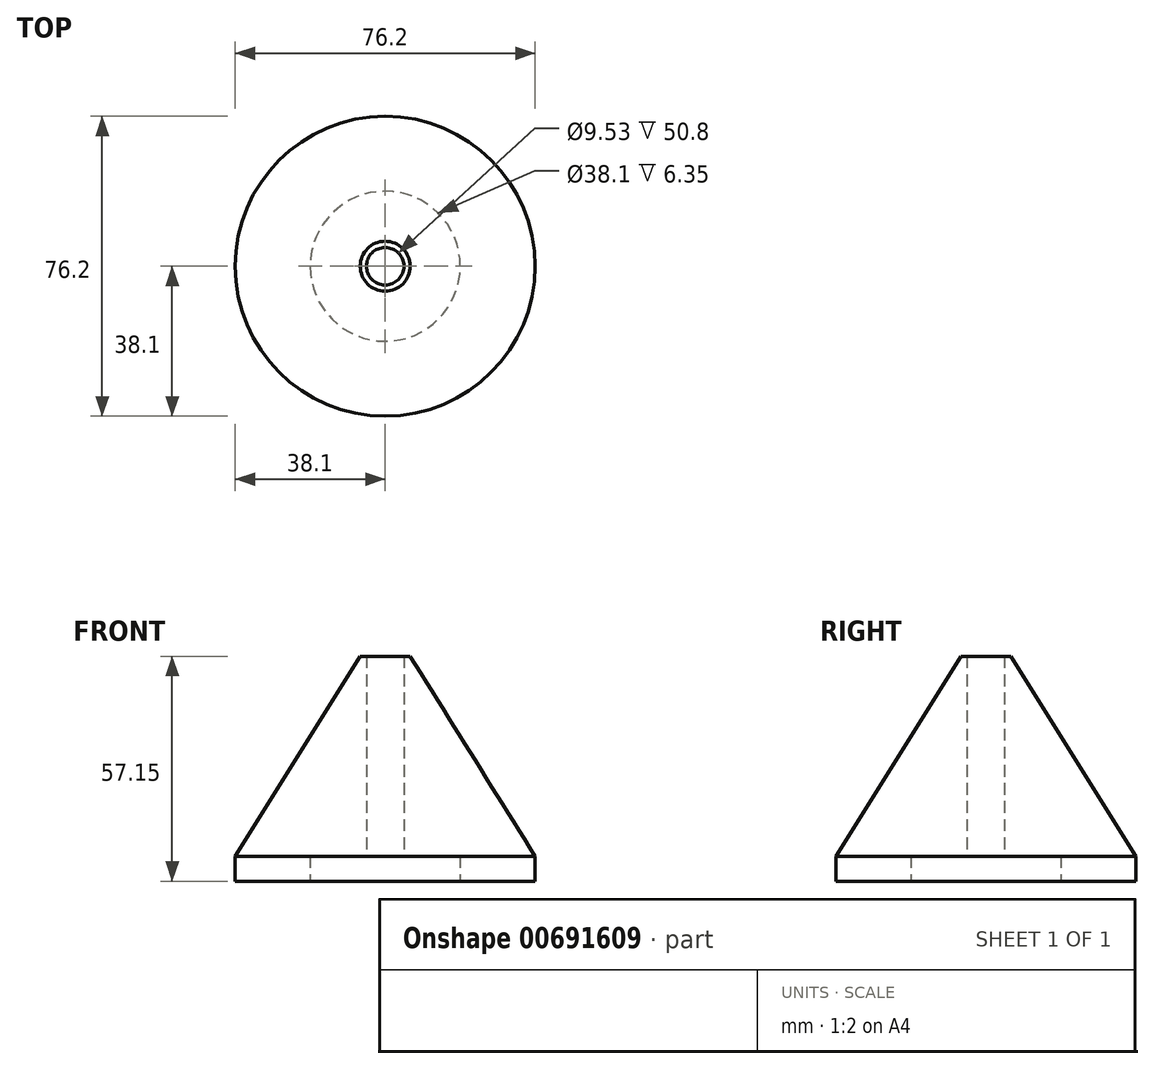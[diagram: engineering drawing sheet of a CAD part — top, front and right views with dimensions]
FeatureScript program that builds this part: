
annotation { "Feature Type Name" : "Feature", "Feature Type Description" : "" }
export const myFeature = defineFeature(function(context is Context, id is Id, definition is map)
    precondition{}
    {
        {
            var Q0;
            Q0=qCreatedBy(makeId("Top.planeOp"),FACE);
            var sketch = newSketch(context, id + "F0", { "sketchPlane" : qUnion([Q0])});
            skCircle(sketch, "E0", {"center": v(0, 0) * mm, "radius": 38.1 * mm});
            skCircle(sketch, "E1", {"center": v(0, 0) * mm, "radius": 4.76 * mm});
            skSolve(sketch);
        }
        {
            var Q0;
            Q0 = qSketchRegion(id + "F0", true);
            extrude(context, id + "F1", {"entities" : qUnion([Q0]), "depth" : 57.15 * mm, "offsetDistance" : 25.4 * mm});
        }
        {
            var Q0;
            Q0=makeQuery(id+"F1.opExtrude","CAP_EDGE",EDGE,{"disambiguationData":[OSD([sQuery(id+"F0.wireOp",EDGE,"E0")])],"isStart":false});
            chamfer(context, id + "F2", {"entities" : qUnion([Q0]), "chamferType" : ChamferType.TWO_OFFSETS, "width1" : 31.75 * mm, "oppositeDirection" : false, "width2" : 50.8 * mm, "tangentPropagation" : true});
        }
        {
            var Q0;
            Q0=makeQuery(id+"F1.opExtrude","CAP_FACE",FACE,{"disambiguationData":[OSD([sQuery(id+"F0.wireOp",EDGE,"E0"),sQuery(id+"F0.wireOp",EDGE,"E1")])],"isStart":true});
            var sketch = newSketch(context, id + "F3", { "sketchPlane" : qUnion([Q0])});
            skSolve(sketch);
        }
        {
            var Q0;
            Q0=makeQuery(id+"F3.imprint","IMPRINT",FACE,{"disambiguationData":[TD([[makeQuery(id+"F3.imprint","IMPRINT",EDGE,{"derivedFrom":makeQuery(id+"F1.opExtrude","CAP_EDGE",EDGE,{"disambiguationData":[OSD([sQuery(id+"F0.wireOp",EDGE,"E0")])],"isStart":true})}),-1.0]])]});
            var sketch = newSketch(context, id + "F4", { "sketchPlane" : qUnion([Q0])});
            skCircle(sketch, "E2", {"center": v(0, 0) * mm, "radius": 19.05 * mm});
            skSolve(sketch);
        }
        {
            var Q0;
            Q0 = qSketchRegion(id + "F4", true);
            extrude(context, id + "F5", {"entities" : qUnion([Q0]), "operationType" : NewBodyOperationType.REMOVE, "oppositeDirection" : true, "depth" : 6.35 * mm, "offsetDistance" : 25.4 * mm});
        }
    });
